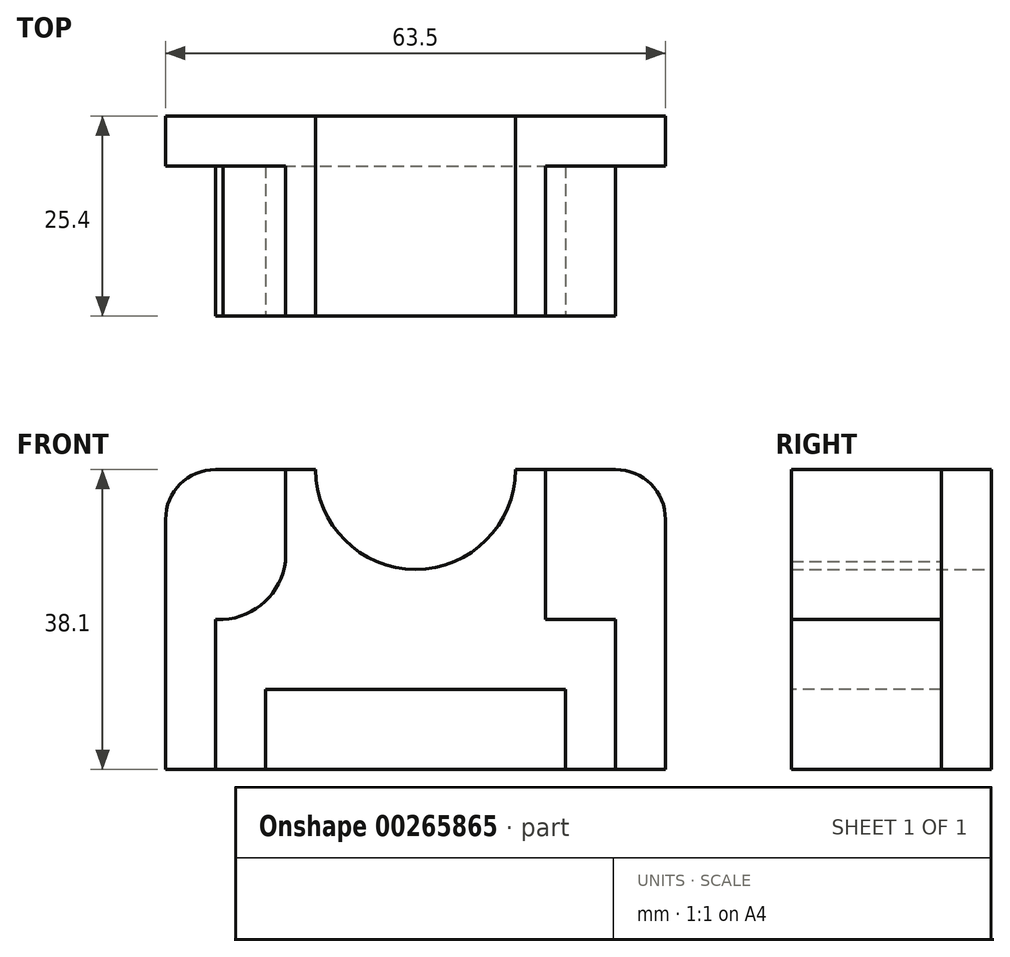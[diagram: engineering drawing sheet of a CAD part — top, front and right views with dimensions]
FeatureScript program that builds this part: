
annotation { "Feature Type Name" : "Feature", "Feature Type Description" : "" }
export const myFeature = defineFeature(function(context is Context, id is Id, definition is map)
    precondition{}
    {
        {
            var Q0;
            Q0=qCreatedBy(makeId("Front.planeOp"),FACE);
            var sketch = newSketch(context, id + "F0", { "sketchPlane" : qUnion([Q0])});
            skLineSegment(sketch, "E0.bottom", {"start": v(-31.75, 19.05) * mm, "end": v(31.75, 19.05) * mm});
            skLineSegment(sketch, "E0.top", {"start": v(-31.75, -19.05) * mm, "end": v(31.75, -19.05) * mm});
            skLineSegment(sketch, "E0.left", {"start": v(-31.75, 19.05) * mm, "end": v(-31.75, -19.05) * mm});
            skLineSegment(sketch, "E0.right", {"start": v(31.75, 19.05) * mm, "end": v(31.75, -19.05) * mm});
            skSolve(sketch);
        }
        {
            var Q0;
            Q0=makeQuery(id+"F0.imprint","IMPRINT",FACE,{"disambiguationData":[TD([[makeQuery(id+"F0.imprint","IMPRINT",EDGE,{"derivedFrom":sQuery(id+"F0.wireOp",EDGE,"E0.bottom")}),-1.0]])]});
            extrude(context, id + "F1", {"entities" : qUnion([Q0]), "depth" : 6.35 * mm});
        }
        {
            var Q0;
            Q0=qCreatedBy(makeId("Front.planeOp"),FACE);
            var sketch = newSketch(context, id + "F2", { "sketchPlane" : qUnion([Q0])});
            skCircle(sketch, "E1", {"center": v(0, 19.05) * mm, "radius": 12.7 * mm});
            skSolve(sketch);
        }
        {
            var Q0;
            Q0=makeQuery(id+"F1.opExtrude","CAP_FACE",FACE,{"disambiguationData":[OSD([sQuery(id+"F0.wireOp",EDGE,"E0.bottom"),sQuery(id+"F0.wireOp",EDGE,"E0.top"),sQuery(id+"F0.wireOp",EDGE,"E0.left"),sQuery(id+"F0.wireOp",EDGE,"E0.right")])],"isStart":false});
            var sketch = newSketch(context, id + "F3", { "sketchPlane" : qUnion([Q0])});
            skLineSegment(sketch, "E2.bottom", {"start": v(-25.4, 19.05) * mm, "end": v(25.4, 19.05) * mm});
            skLineSegment(sketch, "E2.top", {"start": v(-25.4, -19.05) * mm, "end": v(25.4, -19.05) * mm});
            skLineSegment(sketch, "E2.left", {"start": v(-25.4, 19.05) * mm, "end": v(-25.4, -19.05) * mm});
            skLineSegment(sketch, "E2.right", {"start": v(25.4, 19.05) * mm, "end": v(25.4, -19.05) * mm});
            skSolve(sketch);
        }
        {
            var Q0;
            Q0 = qSketchRegion(id + "F3", true);
            extrude(context, id + "F4", {"entities" : qUnion([Q0]), "operationType" : NewBodyOperationType.ADD, "depth" : 19.05 * mm});
        }
        {
            var Q0;
            Q0 = qSketchRegion(id + "F2", true);
            extrude(context, id + "F5", {"entities" : qUnion([Q0]), "operationType" : NewBodyOperationType.REMOVE, "oppositeDirection" : true, "depth" : 38.1 * mm});
        }
        {
            var Q0;
            Q0=qCreatedBy(makeId("Front.planeOp"),FACE);
            var sketch = newSketch(context, id + "F6", { "sketchPlane" : qUnion([Q0])});
            skCircle(sketch, "E3", {"center": v(0, 19.05) * mm, "radius": 12.7 * mm});
            skSolve(sketch);
        }
        {
            var Q0;
            Q0=makeQuery(id+"F6.imprint","IMPRINT",FACE,{"disambiguationData":[TD([[makeQuery(id+"F6.imprint","IMPRINT",EDGE,{"derivedFrom":sQuery(id+"F6.wireOp",EDGE,"E3")}),1.0]])]});
            extrude(context, id + "F7", {"entities" : qUnion([Q0]), "operationType" : NewBodyOperationType.REMOVE, "depth" : 25.4 * mm});
        }
        {
            var Q0;
            Q0=qCreatedBy(makeId("Front.planeOp"),FACE);
            var sketch = newSketch(context, id + "F8", { "sketchPlane" : qUnion([Q0])});
            skLineSegment(sketch, "E4.bottom", {"start": v(-25.4, 19.05) * mm, "end": v(-16.5, 19.05) * mm});
            skLineSegment(sketch, "E4.top", {"start": v(-25.4, 0) * mm, "end": v(-16.5, 0) * mm});
            skLineSegment(sketch, "E4.left", {"start": v(-25.4, 19.05) * mm, "end": v(-25.4, 0) * mm});
            skLineSegment(sketch, "E4.right", {"start": v(-16.5, 19.05) * mm, "end": v(-16.5, 0) * mm});
            skLineSegment(sketch, "E5.bottom", {"start": v(16.51, 19.05) * mm, "end": v(25.4, 19.05) * mm});
            skLineSegment(sketch, "E5.top", {"start": v(16.51, 0) * mm, "end": v(25.4, 0) * mm});
            skLineSegment(sketch, "E5.left", {"start": v(16.51, 19.05) * mm, "end": v(16.51, 0) * mm});
            skLineSegment(sketch, "E5.right", {"start": v(25.4, 19.05) * mm, "end": v(25.4, 0) * mm});
            skSolve(sketch);
        }
        {
            var Q0;
            Q0=makeQuery(id+"F4.opExtrude","CAP_FACE",FACE,{"disambiguationData":[OSD([sQuery(id+"F3.wireOp",EDGE,"E2.bottom"),sQuery(id+"F3.wireOp",EDGE,"E2.top"),sQuery(id+"F3.wireOp",EDGE,"E2.left"),sQuery(id+"F3.wireOp",EDGE,"E2.right")])],"isStart":false});
            var sketch = newSketch(context, id + "F9", { "sketchPlane" : qUnion([Q0])});
            skLineSegment(sketch, "E6.bottom", {"start": v(-25.4, 19.05) * mm, "end": v(-16.5, 19.05) * mm});
            skLineSegment(sketch, "E6.top", {"start": v(-25.4, 0) * mm, "end": v(-16.5, 0) * mm});
            skLineSegment(sketch, "E6.left", {"start": v(-25.4, 19.05) * mm, "end": v(-25.4, 0) * mm});
            skLineSegment(sketch, "E6.right", {"start": v(-16.5, 19.05) * mm, "end": v(-16.5, 0) * mm});
            skLineSegment(sketch, "E7.bottom", {"start": v(16.51, 19.05) * mm, "end": v(25.4, 19.05) * mm});
            skLineSegment(sketch, "E7.top", {"start": v(16.51, 0) * mm, "end": v(25.4, 0) * mm});
            skLineSegment(sketch, "E7.left", {"start": v(16.51, 19.05) * mm, "end": v(16.51, 0) * mm});
            skLineSegment(sketch, "E7.right", {"start": v(25.4, 19.05) * mm, "end": v(25.4, 0) * mm});
            skSolve(sketch);
        }
        {
            var Q0;
            Q0 = qSketchRegion(id + "F9", true);
            extrude(context, id + "F10", {"entities" : qUnion([Q0]), "operationType" : NewBodyOperationType.REMOVE, "oppositeDirection" : true, "depth" : 19.05 * mm});
        }
        {
            var Q0;
            Q0=makeQuery(id+"F4.opExtrude","CAP_FACE",FACE,{"disambiguationData":[OSD([sQuery(id+"F3.wireOp",EDGE,"E2.bottom"),sQuery(id+"F3.wireOp",EDGE,"E2.top"),sQuery(id+"F3.wireOp",EDGE,"E2.left"),sQuery(id+"F3.wireOp",EDGE,"E2.right")])],"isStart":false});
            var sketch = newSketch(context, id + "F11", { "sketchPlane" : qUnion([Q0])});
            skLineSegment(sketch, "E8.bottom", {"start": v(-19.05, -8.9) * mm, "end": v(19.05, -8.89) * mm});
            skLineSegment(sketch, "E8.top", {"start": v(-19.05, -19.05) * mm, "end": v(19.05, -19.05) * mm});
            skLineSegment(sketch, "E8.left", {"start": v(-19.05, -8.9) * mm, "end": v(-19.05, -19.05) * mm});
            skLineSegment(sketch, "E8.right", {"start": v(19.05, -8.89) * mm, "end": v(19.05, -19.05) * mm});
            skSolve(sketch);
        }
        {
            var Q0;
            Q0=makeQuery(id+"F11.imprint","IMPRINT",FACE,{"disambiguationData":[TD([[makeQuery(id+"F11.imprint","IMPRINT",EDGE,{"derivedFrom":sQuery(id+"F11.wireOp",EDGE,"E8.bottom")}),-1.0]])]});
            extrude(context, id + "F12", {"entities" : qUnion([Q0]), "operationType" : NewBodyOperationType.REMOVE, "oppositeDirection" : true, "depth" : 19.05 * mm});
        }
        {
            var Q0;
            {var subQ0=sQuery(id+"F0.wireOp",EDGE,"E0.left");var subQ1=sQuery(id+"F0.wireOp",EDGE,"E0.top");var subQ2=sQuery(id+"F0.wireOp",EDGE,"E0.bottom");Q0=makeQuery(id+"F10.boolean.opBoolean","MERGE",FACE,{"derivedFrom":[makeQuery(id+"F4.boolean.opBoolean","SPLIT",FACE,{"disambiguationData":[TD([makeQuery(id+"F1.opExtrude","SWEPT_FACE",FACE,{"disambiguationData":[OSD([subQ0])]})])],"derivedFrom":makeQuery(id+"F1.opExtrude","CAP_FACE",FACE,{"disambiguationData":[OSD([subQ2,subQ1,subQ0,sQuery(id+"F0.wireOp",EDGE,"E0.right")])],"isStart":false})}),makeQuery(id+"F10.opExtrude","CAP_FACE",FACE,{"disambiguationData":[OSD([sQuery(id+"F9.wireOp",EDGE,"E6.bottom"),sQuery(id+"F9.wireOp",EDGE,"E6.top"),sQuery(id+"F9.wireOp",EDGE,"E6.left"),sQuery(id+"F9.wireOp",EDGE,"E6.right")])],"isStart":false})]});}
            var sketch = newSketch(context, id + "F13", { "sketchPlane" : qUnion([Q0])});
            skCircle(sketch, "E9", {"center": v(-24.92, 8.46) * mm, "radius": 8.47 * mm});
            skLineSegment(sketch, "E10", {"start": v(-25.4, 0) * mm, "end": v(-16.5, 0) * mm});
            skLineSegment(sketch, "E11", {"start": v(-16.5, 0) * mm, "end": v(-16.5, 9.52) * mm});
            skLineSegment(sketch, "E12", {"start": v(-16.5, 9.52) * mm, "end": v(-16.5, 0) * mm});
            skCircle(sketch, "E13", {"center": v(25.4, 8.91) * mm, "radius": 8.91 * mm});
            skLineSegment(sketch, "E14", {"start": v(16.5, 9.17) * mm, "end": v(16.5, 0) * mm});
            skLineSegment(sketch, "E15", {"start": v(16.5, 0) * mm, "end": v(25.63, 0) * mm});
            skSolve(sketch);
        }
        {
            var Q0;
            {var subQ0=sQuery(id+"F13.wireOp",EDGE,"E10");var subQ1=sQuery(id+"F13.wireOp",EDGE,"E9");var subQ2=makeQuery(id+"F13.imprint","INTERSECT",VERTEX,{"derivedFrom":[subQ1,subQ0]});Q0=makeQuery(id+"F13.imprint","IMPRINT",FACE,{"disambiguationData":[TD([[makeQuery(id+"F13.imprint","IMPRINT",EDGE,{"disambiguationData":[TD([[subQ2,-1.0]])],"derivedFrom":subQ1}),-1.0]])]});}
            var Q1;
            {var subQ0=sQuery(id+"F13.wireOp",EDGE,"E14");var subQ1=sQuery(id+"F13.wireOp",EDGE,"E13");var subQ2=makeQuery(id+"F13.imprint","INTERSECT",VERTEX,{"disambiguationData":[OD(1.0)],"derivedFrom":[subQ1,subQ0]});Q1=makeQuery(id+"F13.imprint","IMPRINT",FACE,{"disambiguationData":[TD([[makeQuery(id+"F13.imprint","IMPRINT",EDGE,{"disambiguationData":[TD([[subQ2,-1.0]])],"derivedFrom":subQ1}),-1.0]])]});}
            extrude(context, id + "F14", {"entities" : qUnion([Q0, Q1]), "operationType" : NewBodyOperationType.ADD, "depth" : 19.05 * mm});
        }
        {
            var Q0;
            {var subQ0=sQuery(id+"F0.wireOp",EDGE,"E0.left");var subQ1=sQuery(id+"F0.wireOp",EDGE,"E0.top");var subQ2=sQuery(id+"F0.wireOp",EDGE,"E0.bottom");Q0=makeQuery(id+"F10.boolean.opBoolean","MERGE",FACE,{"derivedFrom":[makeQuery(id+"F4.boolean.opBoolean","SPLIT",FACE,{"disambiguationData":[TD([makeQuery(id+"F1.opExtrude","SWEPT_FACE",FACE,{"disambiguationData":[OSD([subQ0])]})])],"derivedFrom":makeQuery(id+"F1.opExtrude","CAP_FACE",FACE,{"disambiguationData":[OSD([subQ2,subQ1,subQ0,sQuery(id+"F0.wireOp",EDGE,"E0.right")])],"isStart":false})}),makeQuery(id+"F10.opExtrude","CAP_FACE",FACE,{"disambiguationData":[OSD([sQuery(id+"F9.wireOp",EDGE,"E6.bottom"),sQuery(id+"F9.wireOp",EDGE,"E6.top"),sQuery(id+"F9.wireOp",EDGE,"E6.left"),sQuery(id+"F9.wireOp",EDGE,"E6.right")])],"isStart":false})]});}
            var sketch = newSketch(context, id + "F15", { "sketchPlane" : qUnion([Q0])});
            skCircle(sketch, "E16", {"center": v(-25.4, 12.7) * mm, "radius": 6.35 * mm});
            skCircle(sketch, "E17", {"center": v(25.4, 12.7) * mm, "radius": 6.35 * mm});
            skLineSegment(sketch, "E18", {"start": v(-31.75, 12.7) * mm, "end": v(-31.75, 19.05) * mm});
            skLineSegment(sketch, "E19", {"start": v(-31.75, 19.05) * mm, "end": v(-25.4, 19.05) * mm});
            skLineSegment(sketch, "E20", {"start": v(-25.4, 19.05) * mm, "end": v(-31.75, 19.05) * mm});
            skLineSegment(sketch, "E21", {"start": v(25.4, 19.05) * mm, "end": v(31.75, 19.05) * mm});
            skLineSegment(sketch, "E22", {"start": v(31.75, 19.05) * mm, "end": v(31.75, 12.7) * mm});
            skSolve(sketch);
        }
        {
            var Q0;
            {var subQ0=sQuery(id+"F15.wireOp",EDGE,"E18");Q0=makeQuery(id+"F15.imprint","IMPRINT",FACE,{"disambiguationData":[TD([[makeQuery(id+"F15.imprint","IMPRINT",EDGE,{"derivedFrom":subQ0}),1.0]])]});}
            var Q1;
            {var subQ0=sQuery(id+"F15.wireOp",EDGE,"E21");Q1=makeQuery(id+"F15.imprint","IMPRINT",FACE,{"disambiguationData":[TD([[makeQuery(id+"F15.imprint","IMPRINT",EDGE,{"derivedFrom":subQ0}),-1.0]])]});}
            extrude(context, id + "F16", {"entities" : qUnion([Q0, Q1]), "operationType" : NewBodyOperationType.REMOVE, "oppositeDirection" : true, "depth" : 25.4 * mm});
        }
    });
